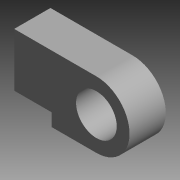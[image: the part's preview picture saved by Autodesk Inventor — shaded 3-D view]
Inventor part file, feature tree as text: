
AUTODESK INVENTOR PART (.ipt)
format: ipt  version: 2014 SP1 (Build 180222100, 222)  size: 89,088 bytes
history: native  units: in
note: dims shown in document units (in); Inventor stores cm internally (conversion verified against a paired STEP export)
features: extrude x1, sketch x1
ambient origin geometry x8: Origin, YZ Plane, XZ Plane, XY Plane, X Axis, Y Axis, Z Axis, Center Point
bodies: Solid1 (feature_tree)
feature tree (2):
  extrude  "Extrusion1"  Depth=0.2228in
  sketch  "Sketch1"  dims[d3=0.2037in d4=0.25in d5=0.2228in d6=0.0in d7=0.2756in d9=0.0787in d10=0.2228in d11=0.0394in d12=0.2228in]
